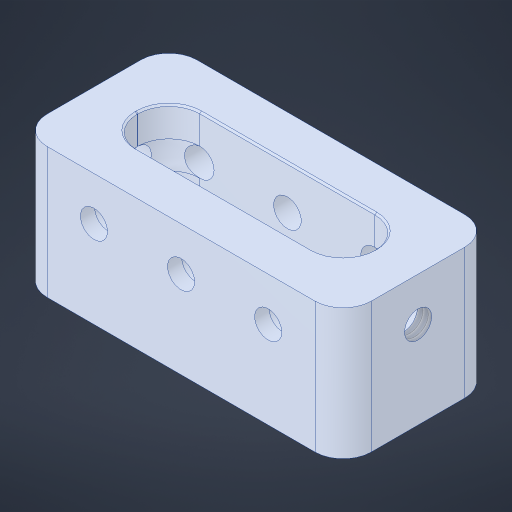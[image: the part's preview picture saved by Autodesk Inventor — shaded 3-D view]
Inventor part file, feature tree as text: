
AUTODESK INVENTOR PART (.ipt)
format: ipt  version: 2023.4 (Build 274418000, 418)  size: 387,072 bytes
history: native  units: in
note: dims shown in document units (in); Inventor stores cm internally (conversion verified against a paired STEP export)
features: sketch x4, hole x3, projected_geometry x2, extrude x1, chamfer x1
ambient origin geometry x8: Origin, YZ Plane, XZ Plane, XY Plane, X Axis, Y Axis, Z Axis, Center Point
bodies: Solid1 (feature_tree)
feature tree (11):
  extrude  "Extrusion1"  Depth=1.0in TaperAngle=0.0deg
  hole  "Hole1"  [1 undecoded]
  hole  "Hole2"  [1 undecoded]
  hole  "Hole3"  [1 undecoded]
  sketch  "Sketch1"  dims[d0=0.0625in d1=1.0in d2=0.0in]
  projected_geometry  "Projected Loop1"
  sketch  "Sketch2"  dims[d3=0.156in d4=0.38in d5=0.385in d6=0.25in d7=0.563in d8=1.0in d9=0.8108in]
  projected_geometry  "Projected Loop2"
  sketch  "Sketch3"  dims[d10=0.196in d11=0.5in d12=0.375in d13=0.25in d14=0.5635in d15=1.0in d16=0.8108in]
  sketch  "Sketch4"  dims[d17=0.156in d18=0.38in d19=0.385in d20=0.25in d21=0.563in d22=1.0in d23=0.8108in d24=1.0in d25=1.0in d26=1.0in d27=0.15in d28=0.25in d29=0.375in d30=32.2835in d31=0.75in d32=46.4567in d33=0.0625in d34=0.75in d35=0.375in]
  chamfer  "Chamfer2"  Distance=0.15in
note: 3 required parameter values undecoded (feature->parameter linkage not recoverable at this tier; creation-order binding heuristic only, values carry confidence <= 0.55)
